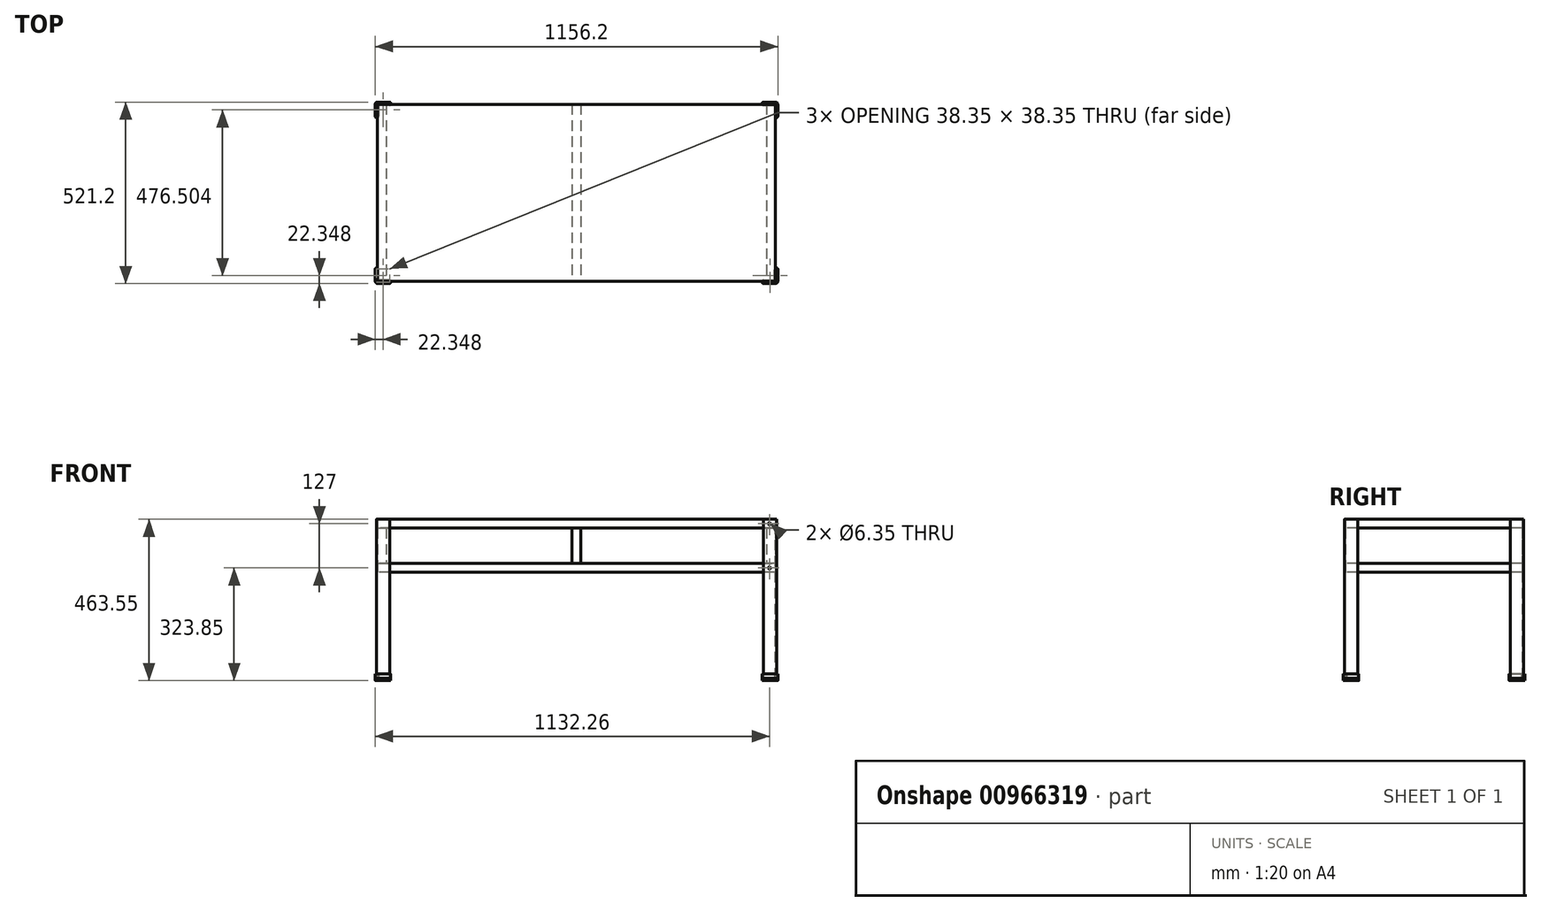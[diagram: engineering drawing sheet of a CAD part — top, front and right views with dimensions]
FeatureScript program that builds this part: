
annotation { "Feature Type Name" : "Feature", "Feature Type Description" : "" }
export const myFeature = defineFeature(function(context is Context, id is Id, definition is map)
    precondition{}
    {
        {
            var Q0;
            Q0=qCreatedBy(makeId("Top.planeOp"),FACE);
            var sketch = newSketch(context, id + "F0", { "sketchPlane" : qUnion([Q0])});
            skLineSegment(sketch, "E0.bottom", {"start": v(571.5, 254) * mm, "end": v(-571.5, 254) * mm});
            skLineSegment(sketch, "E0.top", {"start": v(571.5, -254) * mm, "end": v(-571.5, -254) * mm});
            skLineSegment(sketch, "E0.left", {"start": v(571.5, 254) * mm, "end": v(571.5, -254) * mm});
            skLineSegment(sketch, "E0.right", {"start": v(-571.5, 254) * mm, "end": v(-571.5, -254) * mm});
            skPoint(sketch, "E0.middle", {"position": v(0, 0) * mm});
            skSolve(sketch);
        }
        {
            var Q0;
            Q0 = qSketchRegion(id + "F0", true);
            extrude(context, id + "F1", {"entities" : qUnion([Q0]), "depth" : 25.4 * mm, "offsetDistance" : 25.4 * mm});
        }
        {
            var Q0;
            Q0=makeQuery(id+"F1.opExtrude","CAP_FACE",FACE,{"disambiguationData":[OSD([sQuery(id+"F0.wireOp",EDGE,"E0.bottom"),sQuery(id+"F0.wireOp",EDGE,"E0.top"),sQuery(id+"F0.wireOp",EDGE,"E0.left"),sQuery(id+"F0.wireOp",EDGE,"E0.right")])],"isStart":false});
            var sketch = newSketch(context, id + "F2", { "sketchPlane" : qUnion([Q0])});
            skLineSegment(sketch, "E1.bottom", {"start": v(-571.5, 254) * mm, "end": v(-546.1, 254) * mm});
            skLineSegment(sketch, "E1.top", {"start": v(-571.5, -254) * mm, "end": v(-546.1, -254) * mm});
            skLineSegment(sketch, "E1.left", {"start": v(-571.5, 254) * mm, "end": v(-571.5, -254) * mm});
            skLineSegment(sketch, "E1.right", {"start": v(-546.1, 254) * mm, "end": v(-546.1, -254) * mm});
            skLineSegment(sketch, "E2.bottom", {"start": v(571.5, 254) * mm, "end": v(546.1, 254) * mm});
            skLineSegment(sketch, "E2.top", {"start": v(571.5, -254) * mm, "end": v(546.1, -254) * mm});
            skLineSegment(sketch, "E2.left", {"start": v(571.5, 254) * mm, "end": v(571.5, -254) * mm});
            skLineSegment(sketch, "E2.right", {"start": v(546.1, 254) * mm, "end": v(546.1, -254) * mm});
            skSolve(sketch);
        }
        {
            var Q0;
            Q0 = qSketchRegion(id + "F2", true);
            extrude(context, id + "F3", {"entities" : qUnion([Q0]), "operationType" : NewBodyOperationType.ADD, "depth" : 101.6 * mm, "offsetDistance" : 25.4 * mm});
        }
        {
            var Q0;
            Q0=makeQuery(id+"F3.opExtrude","CAP_FACE",FACE,{"disambiguationData":[OSD([sQuery(id+"F2.wireOp",EDGE,"E1.bottom"),sQuery(id+"F2.wireOp",EDGE,"E1.top"),sQuery(id+"F2.wireOp",EDGE,"E1.left"),sQuery(id+"F2.wireOp",EDGE,"E1.right")])],"isStart":false});
            var sketch = newSketch(context, id + "F4", { "sketchPlane" : qUnion([Q0])});
            skLineSegment(sketch, "E3.bottom", {"start": v(-571.5, 254) * mm, "end": v(571.5, 254) * mm});
            skLineSegment(sketch, "E3.top", {"start": v(-571.5, -254) * mm, "end": v(571.5, -254) * mm});
            skLineSegment(sketch, "E3.left", {"start": v(-571.5, 254) * mm, "end": v(-571.5, -254) * mm});
            skLineSegment(sketch, "E3.right", {"start": v(571.5, 254) * mm, "end": v(571.5, -254) * mm});
            skSolve(sketch);
        }
        {
            var Q0;
            Q0 = qSketchRegion(id + "F4", true);
            extrude(context, id + "F5", {"entities" : qUnion([Q0]), "operationType" : NewBodyOperationType.ADD, "depth" : 25.4 * mm, "offsetDistance" : 25.4 * mm});
        }
        {
            var Q0;
            Q0=makeQuery(id+"F5.boolean.opBoolean","MERGE",FACE,{"derivedFrom":[makeQuery(id+"F3.boolean.opBoolean","MERGE",FACE,{"derivedFrom":[makeQuery(id+"F1.opExtrude","SWEPT_FACE",FACE,{"disambiguationData":[OSD([sQuery(id+"F0.wireOp",EDGE,"E0.top")])]}),makeQuery(id+"F3.opExtrude","SWEPT_FACE",FACE,{"disambiguationData":[OSD([sQuery(id+"F2.wireOp",EDGE,"E1.top")])]}),makeQuery(id+"F3.opExtrude","SWEPT_FACE",FACE,{"disambiguationData":[OSD([sQuery(id+"F2.wireOp",EDGE,"E2.top")])]})]}),makeQuery(id+"F5.opExtrude","SWEPT_FACE",FACE,{"disambiguationData":[OSD([sQuery(id+"F4.wireOp",EDGE,"E3.top")])]})]});
            var sketch = newSketch(context, id + "F6", { "sketchPlane" : qUnion([Q0])});
            skLineSegment(sketch, "E4", {"start": v(-546.1, 127) * mm, "end": v(-571.5, 127) * mm});
            skLineSegment(sketch, "E5", {"start": v(-571.5, 127) * mm, "end": v(-571.5, 126.87) * mm});
            skLineSegment(sketch, "E6", {"start": v(-571.5, 126.87) * mm, "end": v(-546.1, 126.87) * mm});
            skLineSegment(sketch, "E7", {"start": v(-546.1, 126.87) * mm, "end": v(-546.1, 127) * mm});
            skLineSegment(sketch, "E8", {"start": v(0, 205.84) * mm, "end": v(0, -150.4) * mm, "construction": true});
            skPoint(sketch, "E8.startSnap0", {"position": v(0, 152.4) * mm});
            skLineSegment(sketch, "E9", {"start": v(-571.5, 76.2) * mm, "end": v(571.5, 76.2) * mm, "construction": true});
            skLineSegment(sketch, "E10.MirrorCS", {"start": v(546.1, 126.87) * mm, "end": v(546.1, 127) * mm});
            skLineSegment(sketch, "E11.MirrorCS", {"start": v(571.5, 127) * mm, "end": v(571.5, 126.87) * mm});
            skLineSegment(sketch, "E12.MirrorCS", {"start": v(546.1, 127) * mm, "end": v(571.5, 127) * mm});
            skLineSegment(sketch, "E13.MirrorCS", {"start": v(571.5, 126.87) * mm, "end": v(546.1, 126.87) * mm});
            skLineSegment(sketch, "E14.MirrorCS", {"start": v(-571.5, 25.4) * mm, "end": v(-571.5, 25.53) * mm});
            skLineSegment(sketch, "E15.MirrorCS", {"start": v(-546.1, 25.53) * mm, "end": v(-546.1, 25.4) * mm});
            skLineSegment(sketch, "E16.MirrorCS", {"start": v(-546.1, 25.4) * mm, "end": v(-571.5, 25.4) * mm});
            skLineSegment(sketch, "E17.MirrorCS", {"start": v(-571.5, 25.53) * mm, "end": v(-546.1, 25.53) * mm});
            skLineSegment(sketch, "E18.MirrorCS", {"start": v(546.1, 25.53) * mm, "end": v(546.1, 25.4) * mm});
            skLineSegment(sketch, "E19.MirrorCS", {"start": v(571.5, 25.4) * mm, "end": v(571.5, 25.53) * mm});
            skLineSegment(sketch, "E20.MirrorCS", {"start": v(546.1, 25.4) * mm, "end": v(571.5, 25.4) * mm});
            skLineSegment(sketch, "E21.MirrorCS", {"start": v(571.5, 25.53) * mm, "end": v(546.1, 25.53) * mm});
            skSolve(sketch);
        }
        {
            var Q0;
            Q0 = qSketchRegion(id + "F6", true);
            extrude(context, id + "F7", {"entities" : qUnion([Q0]), "operationType" : NewBodyOperationType.REMOVE, "endBound" : BoundingType.THROUGH_ALL, "oppositeDirection" : true, "depth" : 25.4 * mm, "offsetDistance" : 25.4 * mm});
        }
        {
            var Q0;
            Q0=makeQuery(id+"F5.opExtrude","CAP_FACE",FACE,{"disambiguationData":[OSD([sQuery(id+"F4.wireOp",EDGE,"E3.bottom"),sQuery(id+"F4.wireOp",EDGE,"E3.top"),sQuery(id+"F4.wireOp",EDGE,"E3.left"),sQuery(id+"F4.wireOp",EDGE,"E3.right")])],"isStart":false});
            var sketch = newSketch(context, id + "F8", { "sketchPlane" : qUnion([Q0])});
            skLineSegment(sketch, "E22", {"start": v(536.7, -254.13) * mm, "end": v(571.63, -254.13) * mm});
            skLineSegment(sketch, "E23", {"start": v(571.63, -254.13) * mm, "end": v(571.63, -219.2) * mm});
            skLineSegment(sketch, "E24", {"start": v(571.63, -219.2) * mm, "end": v(574.8, -219.2) * mm});
            skLineSegment(sketch, "E25", {"start": v(574.8, -219.2) * mm, "end": v(574.8, -257.3) * mm});
            skLineSegment(sketch, "E26", {"start": v(574.8, -257.3) * mm, "end": v(536.7, -257.3) * mm});
            skLineSegment(sketch, "E27", {"start": v(536.7, -257.3) * mm, "end": v(536.7, -254.13) * mm});
            skLineSegment(sketch, "E28", {"start": v(0, 316) * mm, "end": v(0, -317.65) * mm, "construction": true});
            skPoint(sketch, "E28.startSnap0", {"position": v(0, 254) * mm});
            skPoint(sketch, "E28.endSnap0", {"position": v(0, -254) * mm});
            skLineSegment(sketch, "E29", {"start": v(-611.7, 0) * mm, "end": v(618.75, 0) * mm, "construction": true});
            skLineSegment(sketch, "E30.MirrorCS", {"start": v(571.63, 219.2) * mm, "end": v(574.8, 219.2) * mm});
            skLineSegment(sketch, "E31.MirrorCS", {"start": v(574.8, 219.2) * mm, "end": v(574.8, 257.3) * mm});
            skLineSegment(sketch, "E32.MirrorCS", {"start": v(574.8, 257.3) * mm, "end": v(536.7, 257.3) * mm});
            skLineSegment(sketch, "E33.MirrorCS", {"start": v(571.63, 254.13) * mm, "end": v(571.63, 219.2) * mm});
            skLineSegment(sketch, "E34.MirrorCS", {"start": v(536.7, 257.3) * mm, "end": v(536.7, 254.13) * mm});
            skLineSegment(sketch, "E35.MirrorCS", {"start": v(536.7, 254.13) * mm, "end": v(571.63, 254.13) * mm});
            skLineSegment(sketch, "E36.MirrorCS", {"start": v(-571.63, -219.2) * mm, "end": v(-574.8, -219.2) * mm});
            skLineSegment(sketch, "E37.MirrorCS", {"start": v(-574.8, 219.2) * mm, "end": v(-574.8, 257.3) * mm});
            skLineSegment(sketch, "E38.MirrorCS", {"start": v(-536.7, -257.3) * mm, "end": v(-536.7, -254.13) * mm});
            skLineSegment(sketch, "E39.MirrorCS", {"start": v(-571.63, 219.2) * mm, "end": v(-574.8, 219.2) * mm});
            skLineSegment(sketch, "E40.MirrorCS", {"start": v(-571.63, -254.13) * mm, "end": v(-571.63, -219.2) * mm});
            skLineSegment(sketch, "E41.MirrorCS", {"start": v(-536.7, -254.13) * mm, "end": v(-571.63, -254.13) * mm});
            skLineSegment(sketch, "E42.MirrorCS", {"start": v(-574.8, -257.3) * mm, "end": v(-536.7, -257.3) * mm});
            skLineSegment(sketch, "E43.MirrorCS", {"start": v(-574.8, 257.3) * mm, "end": v(-536.7, 257.3) * mm});
            skLineSegment(sketch, "E44.MirrorCS", {"start": v(-536.7, 254.13) * mm, "end": v(-571.63, 254.13) * mm});
            skLineSegment(sketch, "E45.MirrorCS", {"start": v(-574.8, -219.2) * mm, "end": v(-574.8, -257.3) * mm});
            skLineSegment(sketch, "E46.MirrorCS", {"start": v(-536.7, 257.3) * mm, "end": v(-536.7, 254.13) * mm});
            skLineSegment(sketch, "E47.MirrorCS", {"start": v(-571.63, 254.13) * mm, "end": v(-571.63, 219.2) * mm});
            skSolve(sketch);
        }
        {
            var Q0;
            Q0 = qSketchRegion(id + "F8", true);
            extrude(context, id + "F9", {"entities" : qUnion([Q0]), "oppositeDirection" : true, "depth" : 457.2 * mm, "offsetDistance" : 25.4 * mm});
        }
        {
            var Q0;
            Q0=makeQuery(id+"F9.opExtrude","SWEPT_EDGE",EDGE,{"disambiguationData":[OSD([sQuery(id+"F8.wireOp",EDGE,"E25"),sQuery(id+"F8.wireOp",EDGE,"E26")])]});
            var Q1;
            Q1=makeQuery(id+"F9.opExtrude","SWEPT_EDGE",EDGE,{"disambiguationData":[OSD([sQuery(id+"F8.wireOp",EDGE,"E31.MirrorCS"),sQuery(id+"F8.wireOp",EDGE,"E32.MirrorCS")])]});
            var Q2;
            Q2=makeQuery(id+"F9.opExtrude","SWEPT_EDGE",EDGE,{"disambiguationData":[OSD([sQuery(id+"F8.wireOp",EDGE,"E37.MirrorCS"),sQuery(id+"F8.wireOp",EDGE,"E43.MirrorCS")])]});
            var Q3;
            Q3=makeQuery(id+"F9.opExtrude","SWEPT_EDGE",EDGE,{"disambiguationData":[OSD([sQuery(id+"F8.wireOp",EDGE,"E42.MirrorCS"),sQuery(id+"F8.wireOp",EDGE,"E45.MirrorCS")])]});
            fillet(context, id + "F10", {"entities" : qUnion([Q0, Q1, Q2, Q3]), "tangentPropagation" : true, "radius" : 3.17 * mm, "defaultsChanged" : true, "vertexSettings" : [], "allowEdgeOverflow" : false});
        }
        {
            var Q0;
            Q0=makeQuery(id+"F9.opExtrude","SWEPT_FACE",FACE,{"disambiguationData":[OSD([sQuery(id+"F8.wireOp",EDGE,"E26")])]});
            var sketch = newSketch(context, id + "F11", { "sketchPlane" : qUnion([Q0])});
            skCircle(sketch, "E48", {"center": v(554.16, 139.7) * mm, "radius": 3.18 * mm});
            skPoint(sketch, "E48.centerSnap0", {"position": v(554.16, 152.4) * mm});
            skCircle(sketch, "E49", {"center": v(554.16, 12.7) * mm, "radius": 3.18 * mm});
            skSolve(sketch);
        }
        {
            var Q0;
            Q0 = qSketchRegion(id + "F11", true);
            extrude(context, id + "F12", {"entities" : qUnion([Q0]), "operationType" : NewBodyOperationType.REMOVE, "oppositeDirection" : true, "depth" : 3.17 * mm, "offsetDistance" : 25.4 * mm});
        }
        {
            var Q0;
            Q0=makeQuery(id+"F9.opExtrude","CAP_FACE",FACE,{"disambiguationData":[OSD([sQuery(id+"F8.wireOp",EDGE,"E36.MirrorCS"),sQuery(id+"F8.wireOp",EDGE,"E38.MirrorCS"),sQuery(id+"F8.wireOp",EDGE,"E40.MirrorCS"),sQuery(id+"F8.wireOp",EDGE,"E41.MirrorCS"),sQuery(id+"F8.wireOp",EDGE,"E42.MirrorCS"),sQuery(id+"F8.wireOp",EDGE,"E45.MirrorCS")])],"isStart":false});
            var sketch = newSketch(context, id + "F13", { "sketchPlane" : qUnion([Q0])});
            skArc(sketch, "E50.0", {"start": v(-571.63, 257.43) * mm, "mid": v(-573.96, 256.46) * mm, "end": v(-574.93, 254.13) * mm});
            skLineSegment(sketch, "E50.1", {"start": v(-574.93, 219.08) * mm, "end": v(-574.93, 254.13) * mm});
            skLineSegment(sketch, "E50.2", {"start": v(-536.58, 257.43) * mm, "end": v(-536.58, 254) * mm});
            skLineSegment(sketch, "E50.3", {"start": v(-536.58, 254) * mm, "end": v(-571.5, 254) * mm});
            skLineSegment(sketch, "E50.4", {"start": v(-571.5, 254) * mm, "end": v(-571.5, 219.08) * mm});
            skLineSegment(sketch, "E50.5", {"start": v(-571.63, 257.43) * mm, "end": v(-536.58, 257.43) * mm});
            skLineSegment(sketch, "E50.6", {"start": v(-571.5, 219.08) * mm, "end": v(-574.93, 219.08) * mm});
            skArc(sketch, "E51.0", {"start": v(-571.63, 260.6) * mm, "mid": v(-576.2, 258.7) * mm, "end": v(-578.1, 254.13) * mm});
            skLineSegment(sketch, "E51.1", {"start": v(-578.1, 215.9) * mm, "end": v(-578.1, 254.13) * mm});
            skLineSegment(sketch, "E51.2", {"start": v(-533.4, 260.6) * mm, "end": v(-533.4, 250.83) * mm});
            skLineSegment(sketch, "E51.3", {"start": v(-533.4, 250.83) * mm, "end": v(-568.32, 250.83) * mm});
            skLineSegment(sketch, "E51.4", {"start": v(-568.32, 250.83) * mm, "end": v(-568.32, 215.9) * mm});
            skLineSegment(sketch, "E51.5", {"start": v(-571.63, 260.6) * mm, "end": v(-533.4, 260.6) * mm});
            skLineSegment(sketch, "E51.6", {"start": v(-568.32, 215.9) * mm, "end": v(-578.1, 215.9) * mm});
            skSolve(sketch);
        }
        {
            var Q0;
            Q0 = qSketchRegion(id + "F13", true);
            extrude(context, id + "F14", {"entities" : qUnion([Q0]), "oppositeDirection" : true, "depth" : 12.7 * mm, "offsetDistance" : 25.4 * mm});
        }
        {
            var Q0;
            Q0=makeQuery(id+"F14.opExtrude","SWEPT_EDGE",EDGE,{"disambiguationData":[OSD([sQuery(id+"F13.wireOp",EDGE,"E51.2"),sQuery(id+"F13.wireOp",EDGE,"E51.5")])]});
            var Q1;
            Q1=makeQuery(id+"F14.opExtrude","SWEPT_EDGE",EDGE,{"disambiguationData":[OSD([sQuery(id+"F13.wireOp",EDGE,"E51.2"),sQuery(id+"F13.wireOp",EDGE,"E51.3")])]});
            var Q2;
            Q2=makeQuery(id+"F14.opExtrude","SWEPT_EDGE",EDGE,{"disambiguationData":[OSD([sQuery(id+"F13.wireOp",EDGE,"E51.4"),sQuery(id+"F13.wireOp",EDGE,"E51.6")])]});
            var Q3;
            Q3=makeQuery(id+"F14.opExtrude","SWEPT_EDGE",EDGE,{"disambiguationData":[OSD([sQuery(id+"F13.wireOp",EDGE,"E51.1"),sQuery(id+"F13.wireOp",EDGE,"E51.6")])]});
            fillet(context, id + "F15", {"entities" : qUnion([Q0, Q1, Q2, Q3]), "tangentPropagation" : true, "radius" : 3.17 * mm, "defaultsChanged" : false, "vertexSettings" : [], "allowEdgeOverflow" : false});
        }
        {
            var Q0;
            Q0=makeQuery(id+"F14.opExtrude","CAP_FACE",FACE,{"disambiguationData":[OSD([sQuery(id+"F13.wireOp",EDGE,"E50.0"),sQuery(id+"F13.wireOp",EDGE,"E50.1"),sQuery(id+"F13.wireOp",EDGE,"E50.2"),sQuery(id+"F13.wireOp",EDGE,"E50.3"),sQuery(id+"F13.wireOp",EDGE,"E50.4"),sQuery(id+"F13.wireOp",EDGE,"E50.5"),sQuery(id+"F13.wireOp",EDGE,"E50.6"),sQuery(id+"F13.wireOp",EDGE,"E51.0"),sQuery(id+"F13.wireOp",EDGE,"E51.1"),sQuery(id+"F13.wireOp",EDGE,"E51.2"),sQuery(id+"F13.wireOp",EDGE,"E51.3"),sQuery(id+"F13.wireOp",EDGE,"E51.4"),sQuery(id+"F13.wireOp",EDGE,"E51.5"),sQuery(id+"F13.wireOp",EDGE,"E51.6")])],"isStart":true});
            var sketch = newSketch(context, id + "F16", { "sketchPlane" : qUnion([Q0])});
            skLineSegment(sketch, "E52.0", {"start": v(-536.58, 250.83) * mm, "end": v(-568.32, 250.83) * mm});
            skArc(sketch, "E53.0", {"start": v(-536.58, 250.83) * mm, "mid": v(-534.33, 251.75) * mm, "end": v(-533.4, 254) * mm});
            skPoint(sketch, "E54.0", {"position": v(-533.4, 255.71) * mm});
            skLineSegment(sketch, "E55.0", {"start": v(-533.4, 257.43) * mm, "end": v(-533.4, 254) * mm});
            skArc(sketch, "E56.0", {"start": v(-533.4, 257.43) * mm, "mid": v(-534.33, 259.67) * mm, "end": v(-536.58, 260.6) * mm});
            skLineSegment(sketch, "E57.0", {"start": v(-571.63, 260.6) * mm, "end": v(-536.58, 260.6) * mm});
            skArc(sketch, "E58.0", {"start": v(-571.63, 260.6) * mm, "mid": v(-576.2, 258.7) * mm, "end": v(-578.1, 254.13) * mm});
            skLineSegment(sketch, "E59.0", {"start": v(-578.1, 219.08) * mm, "end": v(-578.1, 254.13) * mm});
            skArc(sketch, "E60.0", {"start": v(-578.1, 219.08) * mm, "mid": v(-577.17, 216.83) * mm, "end": v(-574.93, 215.9) * mm});
            skPoint(sketch, "E61.0", {"position": v(-573.21, 215.9) * mm});
            skLineSegment(sketch, "E62.0", {"start": v(-571.5, 215.9) * mm, "end": v(-574.93, 215.9) * mm});
            skArc(sketch, "E63.0", {"start": v(-571.5, 215.9) * mm, "mid": v(-569.25, 216.83) * mm, "end": v(-568.32, 219.08) * mm});
            skLineSegment(sketch, "E64.0", {"start": v(-568.32, 250.83) * mm, "end": v(-568.32, 219.08) * mm});
            skSolve(sketch);
        }
        {
            var Q0;
            Q0 = qSketchRegion(id + "F16", true);
            extrude(context, id + "F17", {"entities" : qUnion([Q0]), "depth" : 6.35 * mm, "offsetDistance" : 25.4 * mm});
        }
        {
            var Q0;
            Q0=makeQuery(id+"F14.opExtrude","SWEPT_BODY",BODY,{"disambiguationData":[OSD([sQuery(id+"F13.wireOp",EDGE,"E50.0"),sQuery(id+"F13.wireOp",EDGE,"E50.1"),sQuery(id+"F13.wireOp",EDGE,"E50.2"),sQuery(id+"F13.wireOp",EDGE,"E50.3"),sQuery(id+"F13.wireOp",EDGE,"E50.4"),sQuery(id+"F13.wireOp",EDGE,"E50.5"),sQuery(id+"F13.wireOp",EDGE,"E50.6"),sQuery(id+"F13.wireOp",EDGE,"E51.0"),sQuery(id+"F13.wireOp",EDGE,"E51.1"),sQuery(id+"F13.wireOp",EDGE,"E51.2"),sQuery(id+"F13.wireOp",EDGE,"E51.3"),sQuery(id+"F13.wireOp",EDGE,"E51.4"),sQuery(id+"F13.wireOp",EDGE,"E51.5"),sQuery(id+"F13.wireOp",EDGE,"E51.6")])]});
            var Q1;
            Q1=qCreatedBy(makeId("Front.planeOp"),FACE);
            mirror(context, id + "F18", {"entities" : qUnion([Q0]), "mirrorPlane" : qUnion([Q1])});
        }
        {
            var Q0;
            Q0=makeQuery(id+"F14.opExtrude","SWEPT_BODY",BODY,{"disambiguationData":[OSD([sQuery(id+"F13.wireOp",EDGE,"E50.0"),sQuery(id+"F13.wireOp",EDGE,"E50.1"),sQuery(id+"F13.wireOp",EDGE,"E50.2"),sQuery(id+"F13.wireOp",EDGE,"E50.3"),sQuery(id+"F13.wireOp",EDGE,"E50.4"),sQuery(id+"F13.wireOp",EDGE,"E50.5"),sQuery(id+"F13.wireOp",EDGE,"E50.6"),sQuery(id+"F13.wireOp",EDGE,"E51.0"),sQuery(id+"F13.wireOp",EDGE,"E51.1"),sQuery(id+"F13.wireOp",EDGE,"E51.2"),sQuery(id+"F13.wireOp",EDGE,"E51.3"),sQuery(id+"F13.wireOp",EDGE,"E51.4"),sQuery(id+"F13.wireOp",EDGE,"E51.5"),sQuery(id+"F13.wireOp",EDGE,"E51.6")])]});
            var Q1;
            Q1=qCreatedBy(makeId("Right.planeOp"),FACE);
            mirror(context, id + "F19", {"entities" : qUnion([Q0]), "mirrorPlane" : qUnion([Q1])});
        }
        {
            var Q0;
            Q0=makeQuery(id+"F17.opExtrude","SWEPT_BODY",BODY,{"disambiguationData":[OSD([sQuery(id+"F16.wireOp",EDGE,"E52.0"),sQuery(id+"F16.wireOp",EDGE,"E53.0"),sQuery(id+"F16.wireOp",EDGE,"E55.0"),sQuery(id+"F16.wireOp",EDGE,"E56.0"),sQuery(id+"F16.wireOp",EDGE,"E57.0"),sQuery(id+"F16.wireOp",EDGE,"E58.0"),sQuery(id+"F16.wireOp",EDGE,"E59.0"),sQuery(id+"F16.wireOp",EDGE,"E60.0"),sQuery(id+"F16.wireOp",EDGE,"E62.0"),sQuery(id+"F16.wireOp",EDGE,"E63.0"),sQuery(id+"F16.wireOp",EDGE,"E64.0")])]});
            var Q1;
            Q1=qCreatedBy(makeId("Right.planeOp"),FACE);
            mirror(context, id + "F20", {"entities" : qUnion([Q0]), "mirrorPlane" : qUnion([Q1])});
        }
        {
            var Q0;
            Q0=makeQuery(id+"F17.opExtrude","SWEPT_BODY",BODY,{"disambiguationData":[OSD([sQuery(id+"F16.wireOp",EDGE,"E52.0"),sQuery(id+"F16.wireOp",EDGE,"E53.0"),sQuery(id+"F16.wireOp",EDGE,"E55.0"),sQuery(id+"F16.wireOp",EDGE,"E56.0"),sQuery(id+"F16.wireOp",EDGE,"E57.0"),sQuery(id+"F16.wireOp",EDGE,"E58.0"),sQuery(id+"F16.wireOp",EDGE,"E59.0"),sQuery(id+"F16.wireOp",EDGE,"E60.0"),sQuery(id+"F16.wireOp",EDGE,"E62.0"),sQuery(id+"F16.wireOp",EDGE,"E63.0"),sQuery(id+"F16.wireOp",EDGE,"E64.0")])]});
            var Q1;
            Q1=makeQuery(id+"F20.opPattern","COPY",BODY,{"derivedFrom":makeQuery(id+"F17.opExtrude","SWEPT_BODY",BODY,{"disambiguationData":[OSD([sQuery(id+"F16.wireOp",EDGE,"E52.0"),sQuery(id+"F16.wireOp",EDGE,"E53.0"),sQuery(id+"F16.wireOp",EDGE,"E55.0"),sQuery(id+"F16.wireOp",EDGE,"E56.0"),sQuery(id+"F16.wireOp",EDGE,"E57.0"),sQuery(id+"F16.wireOp",EDGE,"E58.0"),sQuery(id+"F16.wireOp",EDGE,"E59.0"),sQuery(id+"F16.wireOp",EDGE,"E60.0"),sQuery(id+"F16.wireOp",EDGE,"E62.0"),sQuery(id+"F16.wireOp",EDGE,"E63.0"),sQuery(id+"F16.wireOp",EDGE,"E64.0")])]}),"instanceName":"1"});
            var Q2;
            Q2=qCreatedBy(makeId("Front.planeOp"),FACE);
            mirror(context, id + "F21", {"entities" : qUnion([Q0, Q1]), "mirrorPlane" : qUnion([Q2])});
        }
        {
            var Q0;
            {var subQ2=sQuery(id+"F4.wireOp",EDGE,"E3.top");Q0=makeQuery(id+"F7.boolean.opBoolean","SPLIT",FACE,{"disambiguationData":[TD([makeQuery(id+"F7.opExtrude","SWEPT_FACE",FACE,{"disambiguationData":[OSD([sQuery(id+"F6.wireOp",EDGE,"E4")])]})])],"derivedFrom":makeQuery(id+"F5.boolean.opBoolean","MERGE",FACE,{"derivedFrom":[makeQuery(id+"F3.boolean.opBoolean","MERGE",FACE,{"derivedFrom":[makeQuery(id+"F1.opExtrude","SWEPT_FACE",FACE,{"disambiguationData":[OSD([sQuery(id+"F0.wireOp",EDGE,"E0.top")])]}),makeQuery(id+"F3.opExtrude","SWEPT_FACE",FACE,{"disambiguationData":[OSD([sQuery(id+"F2.wireOp",EDGE,"E1.top")])]}),makeQuery(id+"F3.opExtrude","SWEPT_FACE",FACE,{"disambiguationData":[OSD([sQuery(id+"F2.wireOp",EDGE,"E2.top")])]})]}),makeQuery(id+"F5.opExtrude","SWEPT_FACE",FACE,{"disambiguationData":[OSD([subQ2])]})]})});}
            var sketch = newSketch(context, id + "F22", { "sketchPlane" : qUnion([Q0])});
            skLineSegment(sketch, "E65", {"start": v(0, 186) * mm, "end": v(0, -110.7) * mm, "construction": true});
            skPoint(sketch, "E65.startSnap0", {"position": v(0, 152.4) * mm});
            skPoint(sketch, "E65.endSnap0", {"position": v(0, 127) * mm});
            skLineSegment(sketch, "E66", {"start": v(0, 126.87) * mm, "end": v(-12.7, 126.87) * mm});
            skLineSegment(sketch, "E67", {"start": v(-12.7, 126.87) * mm, "end": v(-12.7, 25.53) * mm});
            skLineSegment(sketch, "E68", {"start": v(-12.7, 25.53) * mm, "end": v(0, 25.53) * mm});
            skLineSegment(sketch, "E69.MirrorCS", {"start": v(12.7, 126.87) * mm, "end": v(12.7, 25.53) * mm});
            skLineSegment(sketch, "E70", {"start": v(12.7, 25.53) * mm, "end": v(0, 25.53) * mm});
            skLineSegment(sketch, "E71", {"start": v(0, 126.87) * mm, "end": v(12.7, 126.87) * mm});
            skSolve(sketch);
        }
        {
            var Q0;
            Q0 = qSketchRegion(id + "F22", true);
            var Q1;
            {var subQ3=sQuery(id+"F4.wireOp",EDGE,"E3.bottom");Q1=makeQuery(id+"F7.boolean.opBoolean","SPLIT",FACE,{"disambiguationData":[TD([makeQuery(id+"F7.opExtrude","SWEPT_FACE",FACE,{"disambiguationData":[OSD([sQuery(id+"F6.wireOp",EDGE,"E4")])]})])],"derivedFrom":makeQuery(id+"F5.boolean.opBoolean","MERGE",FACE,{"derivedFrom":[makeQuery(id+"F3.boolean.opBoolean","MERGE",FACE,{"derivedFrom":[makeQuery(id+"F1.opExtrude","SWEPT_FACE",FACE,{"disambiguationData":[OSD([sQuery(id+"F0.wireOp",EDGE,"E0.bottom")])]}),makeQuery(id+"F3.opExtrude","SWEPT_FACE",FACE,{"disambiguationData":[OSD([sQuery(id+"F2.wireOp",EDGE,"E1.bottom")])]}),makeQuery(id+"F3.opExtrude","SWEPT_FACE",FACE,{"disambiguationData":[OSD([sQuery(id+"F2.wireOp",EDGE,"E2.bottom")])]})]}),makeQuery(id+"F5.opExtrude","SWEPT_FACE",FACE,{"disambiguationData":[OSD([subQ3])]})]})});}
            extrude(context, id + "F23", {"entities" : qUnion([Q0]), "endBound" : BoundingType.UP_TO_SURFACE, "oppositeDirection" : true, "depth" : 25.4 * mm, "endBoundEntityFace" : qUnion([Q1]), "offsetDistance" : 25.4 * mm});
        }
    });
